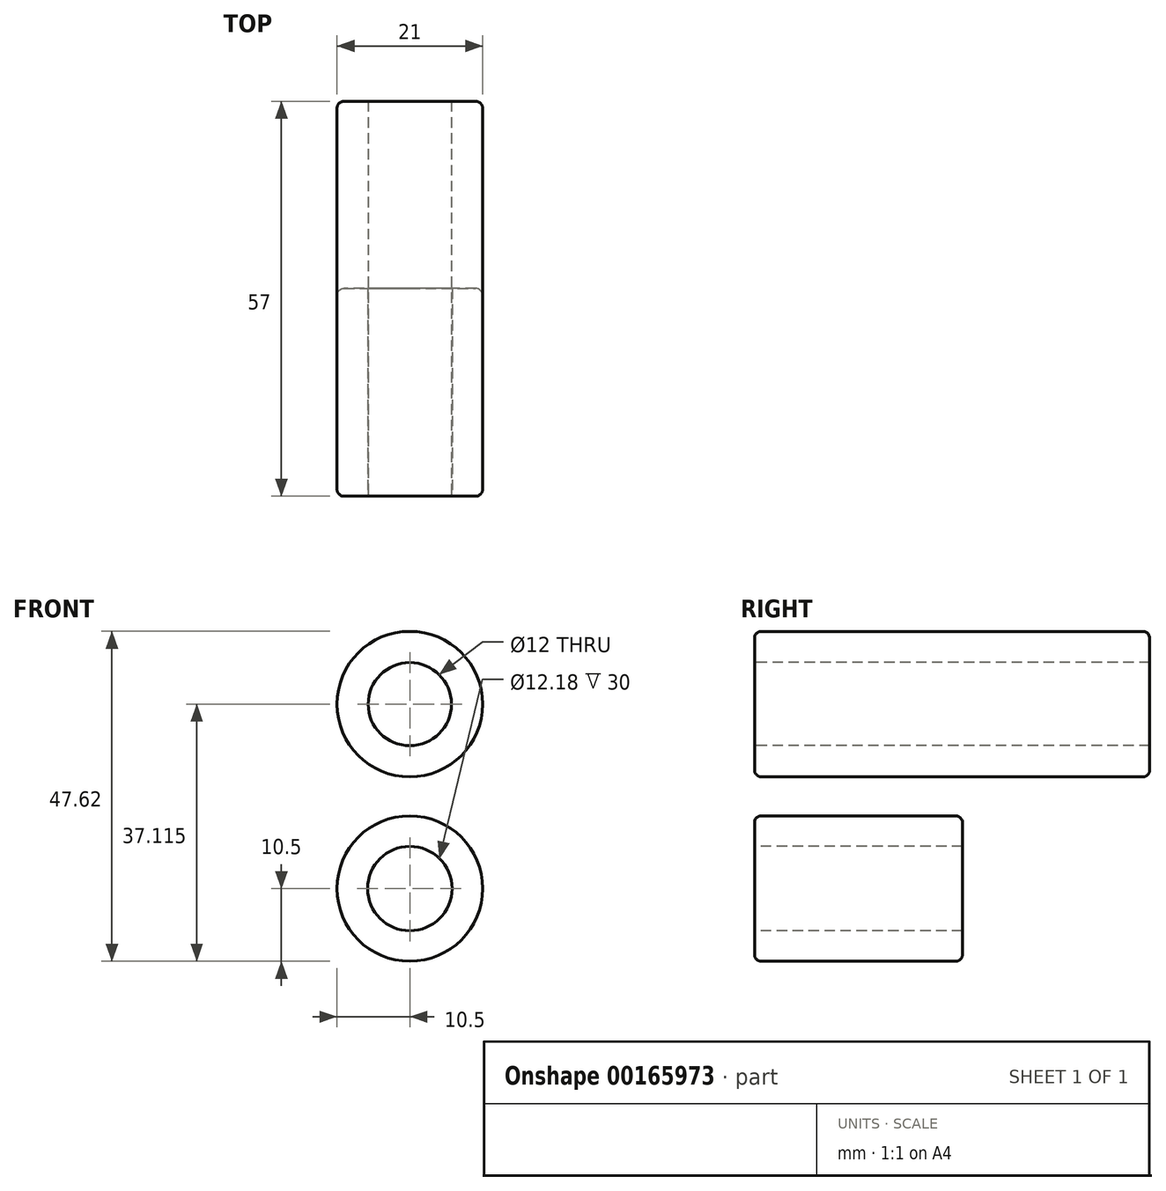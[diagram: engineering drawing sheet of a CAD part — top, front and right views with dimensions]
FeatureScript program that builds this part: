
annotation { "Feature Type Name" : "Feature", "Feature Type Description" : "" }
export const myFeature = defineFeature(function(context is Context, id is Id, definition is map)
    precondition{}
    {
        {
            var Q0;
            Q0=qCreatedBy(makeId("Front.planeOp"),FACE);
            var sketch = newSketch(context, id + "F0", { "sketchPlane" : qUnion([Q0])});
            skCircle(sketch, "E0", {"center": v(0, 0) * mm, "radius": 6.1 * mm});
            skCircle(sketch, "E1", {"center": v(0, 0) * mm, "radius": 10.5 * mm});
            skSolve(sketch);
        }
        {
            var Q0;
            Q0 = qSketchRegion(id + "F0", true);
            extrude(context, id + "F1", {"entities" : qUnion([Q0]), "oppositeDirection" : true, "depth" : 30 * mm});
        }
        {
            var Q0;
            Q0=qCreatedBy(makeId("Front.planeOp"),FACE);
            var sketch = newSketch(context, id + "F2", { "sketchPlane" : qUnion([Q0])});
            skCircle(sketch, "E2", {"center": v(0, 26.62) * mm, "radius": 6 * mm});
            skCircle(sketch, "E3", {"center": v(0, 26.62) * mm, "radius": 10.5 * mm});
            skSolve(sketch);
        }
        {
            var Q0;
            Q0 = qSketchRegion(id + "F2", true);
            extrude(context, id + "F3", {"entities" : qUnion([Q0]), "oppositeDirection" : true, "depth" : 57 * mm});
        }
        {
            var Q0;
            Q0=makeQuery(id+"F3.opExtrude","CAP_EDGE",EDGE,{"disambiguationData":[OSD([sQuery(id+"F2.wireOp",EDGE,"E3")])],"isStart":true});
            var Q1;
            Q1=makeQuery(id+"F1.opExtrude","CAP_EDGE",EDGE,{"disambiguationData":[OSD([sQuery(id+"F0.wireOp",EDGE,"E1")])],"isStart":true});
            var Q2;
            Q2=makeQuery(id+"F1.opExtrude","CAP_EDGE",EDGE,{"disambiguationData":[OSD([sQuery(id+"F0.wireOp",EDGE,"E1")])],"isStart":false});
            var Q3;
            Q3=makeQuery(id+"F3.opExtrude","CAP_EDGE",EDGE,{"disambiguationData":[OSD([sQuery(id+"F2.wireOp",EDGE,"E3")])],"isStart":false});
            fillet(context, id + "F4", {"entities" : qUnion([Q0, Q1, Q2, Q3]), "radius" : 1 * mm, "tangentPropagation" : true, "allowEdgeOverflow" : false});
        }
    });
